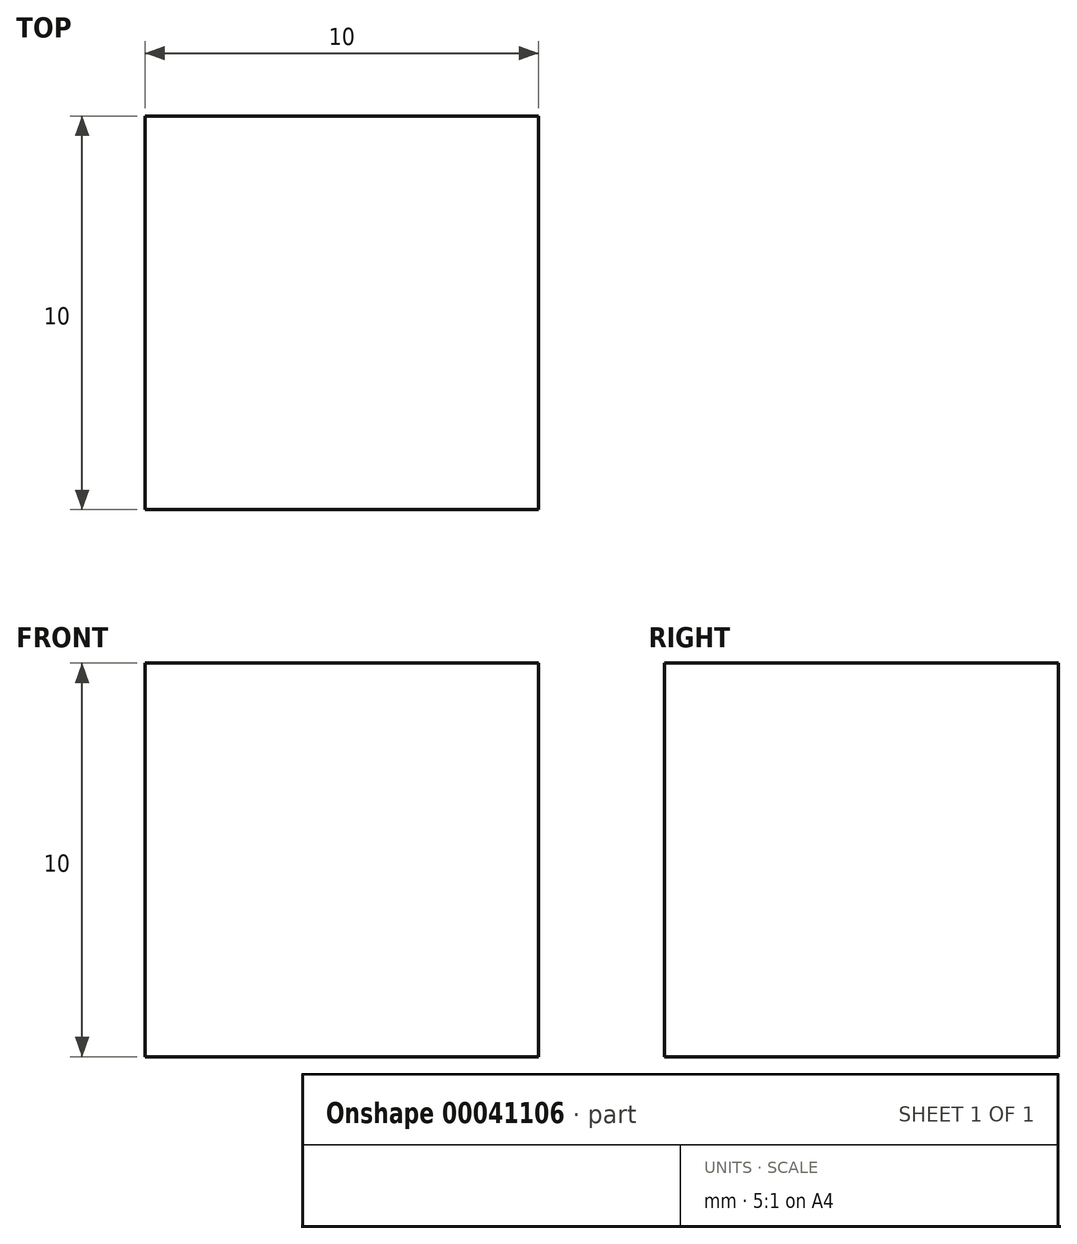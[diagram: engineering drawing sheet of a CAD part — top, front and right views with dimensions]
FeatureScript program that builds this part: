
annotation { "Feature Type Name" : "Feature", "Feature Type Description" : "" }
export const myFeature = defineFeature(function(context is Context, id is Id, definition is map)
    precondition{}
    {
        {
            var Q0;
            Q0=qCreatedBy(makeId("Top.planeOp"),FACE);
            var sketch = newSketch(context, id + "F0", { "sketchPlane" : qUnion([Q0])});
            skLineSegment(sketch, "E0.rect.bottom", {"start": v(5, 5) * mm, "end": v(-5, 5) * mm});
            skLineSegment(sketch, "E0.rect.top", {"start": v(5, -5) * mm, "end": v(-5, -5) * mm});
            skLineSegment(sketch, "E0.rect.left", {"start": v(5, 5) * mm, "end": v(5, -5) * mm});
            skLineSegment(sketch, "E0.rect.right", {"start": v(-5, 5) * mm, "end": v(-5, -5) * mm});
            skPoint(sketch, "E0.rect.middle", {"position": v(0, 0) * mm});
            skSolve(sketch);
        }
        {
            var Q0;
            Q0=makeQuery(id+"F0.imprint","IMPRINT",FACE,{"disambiguationData":[TD([[makeQuery(id+"F0.imprint","IMPRINT",EDGE,{"derivedFrom":sQuery(id+"F0.wireOp",EDGE,"E0.rect.bottom")}),1.0]])]});
            extrude(context, id + "F1", {"entities" : qUnion([Q0]), "depth" : 10 * mm});
        }
    });
